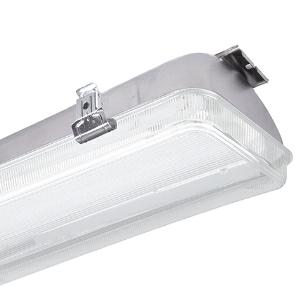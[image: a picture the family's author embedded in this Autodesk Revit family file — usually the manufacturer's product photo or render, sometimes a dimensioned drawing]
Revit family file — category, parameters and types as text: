
# Revit family: 3f_filippi_-_beta_235_92_pc_ampio_3f_filippi_-_52870_-_beta_235_led_921x50_ampio_l1265
name_source: partatom
category: Lighting Fixtures
units: mm (PartAtom-declared; Revit-internal decimal feet)

## family parameters
Cut with Voids When Loaded = No
Host = Face
Light Source = No
Part Type = Normal
Room Calculation Point = No
Round Connector Dimension = Use Diameter
Shared = No

## types (1)
- 3F Filippi - Beta 235 92 PC Ampio (1 x LED, 8036 lm, 54 W, 4000 K)
    Apparent Load = 54 VA
    Approval mark = CE
    CIE Flux Codes = 60 88 98 97 100
    Color Rendering = 80
    Color Temperature = 4000 K
    Control Gear = Electronic ballast
    Default Elevation = 1800 mm
    Description = ILLUMINOTECHNICAL
Luminous efficiency 100% (DLOR 99%, ULOR 1%).
Initial luminous flux of the luminaire 8036 lm.
Wide symmetric distribution.
Installation Interdistance Transv.D = 1.25 x hu - Long.D = 1.44 x hu.
Tabular UGR (CIE 117 - 4H-8H; S=0.25H; 70/50/20): RUG 19.3 - 19.9.
Beam angle: 91° - 102°.
Luminous efficacy 149 lm/W.
Lifetime (L93/B10): 30000 h. (tq+25°C)
Lifetime (L90/B10): 50000 h. (tq+25°C)
Lifetime (L85/B10): 80000 h. (tq+25°C)
Lifetime (L80/B10): 100000 h. (tq+25°C)
Lifetime (L85/B10): 50000 h. (tq+45°C)
Sudden decreased luminous flux after 50000 hours: 0% (C0).
Photobiological safety in compliance with IEC/TR 62778: RG0 risk exempt, (IEC 62471).
In compliance with IEC/EN 62722-2-1 - IEC/EN 62717 standards.

SOURCE
Linear LED module 50W/840.
Energy efficiency class (UE 2019/2020 - UE 2019/2015): C.
CIE 13.3 Colour rendering index: CRI >80 (R9 <50%).
IES TM-30 Fidelity Index: Rf = 84 Rg = 95.
CCT nominal colour temperature 4000 K.
Colour initial tolerance (MacAdam): SDCM 3.

MECHANICAL
Housing in AISI 304 stainless steel, pressed in one single piece.
Polycarbonate screen etched internally, V2 self-extinguishing, UV stabilised, injection moulded.
Ecologic anti-aging sealing gasket.
Oversized gear-tray reflector unit in highly reflective white painted hot-galvanised steel.
Methacrylate (PMMA) lenses with external flat surface.
Stainless steel snap-lock clips for diffuser mounting (safety n° 4 per fixture).
Luminaire with limited surface temperature. - D - (EN 60598-2-24)
Dimensions: 1265x235 mm, height 135 mm. Weight 6.29 kg.
IP65 protection degree.
Mechanical strength to impacts IK10 (20 joule).
Glow-wire test resistance 850°C.

ELECTRICAL
Halogen Free electronic wiring 230V-50/60Hz, power factor 0.95, THD <25%, constant output current, class I, 1 driver.
Power of the luminaire 54 W.
ENEC - CE.
Flicker: <4%.
Luminaire compliant with EN 60598-2-22 for power supply from a centralised emergency system CPSS (Central Power Supply System), not incorporated in the luminaire - high risk areas excluded. The default power and flux are 100% in AC and 100% in DC.
Ambient temperature from -20°C to +45°C.
Temperature class T6 max 85°C.
Quick connection via M20 3P connector with 9-13 mm tightening range.
Relative humidity UR: <85%.

INSTALLATION
Ceiling / Suspended / Wall.
All accessories dedicated to this product are available on the Catalog and on our website www.3F-Filippi.com.

APPLICATIONS
Suitable product for food production plants (HACCP), IFS (Food Version 6), BRC (GSFS Food Version 7).
Dry, dusty indoor environments, subject to occasional water splashes.
Any environments except the ones where the luminaire materials are unsuitable.
Industrial environments, warehouses, environments where security locks are required on all clips, e.g. prisons (on request).
Environments in which it is necessary a total protection against falling fragments (eg environments with foodstuffs or machines with moving parts or with extreme temperature changes), use luminaires with laminated glass.
Tempered glass is not immune to falling fragments from harmless and caused by shocks or exceptionally derived from the tempering process.

WARNING
Fixture not suitable for cold stores with an ambient temperature <0°C and/or relative humidity >85%.
Luminaire designed for disposal/recycling at end-of-life.
Replaceable (LED only) light source by a professional. Replaceable control gear by a professional.
    Height = 135 mm
    Lamp = 1 x LED
    Lamp Light Flux = 8036 lm
    Lamp Power = 54 W
    Lamp count = 1
    Length = 1265 mm
    Lifetime = 50000 h
    Luminous efficacy = 149 lm/W
    Manufacturer = 3F Filippi
    ModVariant = No
    Model = 3F Filippi - 52870 - Beta 235 LED 921x50 AMPIO L1265
    Mounting Place = Ceiling
    Mounting Type = Pendant
    Number of Poles = 1
    OnlyDefault = Yes
    Power Factor = 1
    Product Name = 3F Filippi - Beta 235 92 PC Ampio
    Product group = pendant luminaire
    ProductGroupID = 9
    Protection Class = Protection class I
    Protection Degree = IP 65
    RLX_Detail_Level = 1
    RLX_Emergency_Light_Flux = 0 lm
    RLX_Emergency_Type = 0
    RLX_Emergency_Type_DB = No
    RlxData = <blob elided: 91837 chars, md5=a4e9be40>
    Socket = socket
    Standby Power = 0 W
    System Light Flux = 8036 lm
    System Power = 54 W
    Type Comments = Product without accessories
    Type Image = 3ffilippi_52870.jpg
    URL = http://relux.com
    VarID = ---
    Voltage = 0 V
    Weight = 0.00 kg
    Width = 235 mm

## geometry (parser evidence)
native form markers: Blend x4, Sweep x11
no freeform markers — native parametric forms only
